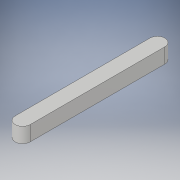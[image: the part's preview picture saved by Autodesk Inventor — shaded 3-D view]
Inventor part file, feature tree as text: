
AUTODESK INVENTOR PART (.ipt)
format: ipt  version: 2017 (Build 210142000, 142)  size: 105,984 bytes
history: native  units: in
note: dims shown in document units (in); Inventor stores cm internally (conversion verified against a paired STEP export)
features: fillet x1
ambient origin geometry x8: Origin, YZ Plane, XZ Plane, XY Plane, X Axis, Y Axis, Z Axis, Center Point
bodies: Solid1 (feature_tree)
feature tree (1):
  fillet  "Fillet1"  [1 undecoded]
note: 1 required parameter value undecoded (feature->parameter linkage not recoverable at this tier; creation-order binding heuristic only, values carry confidence <= 0.55)
